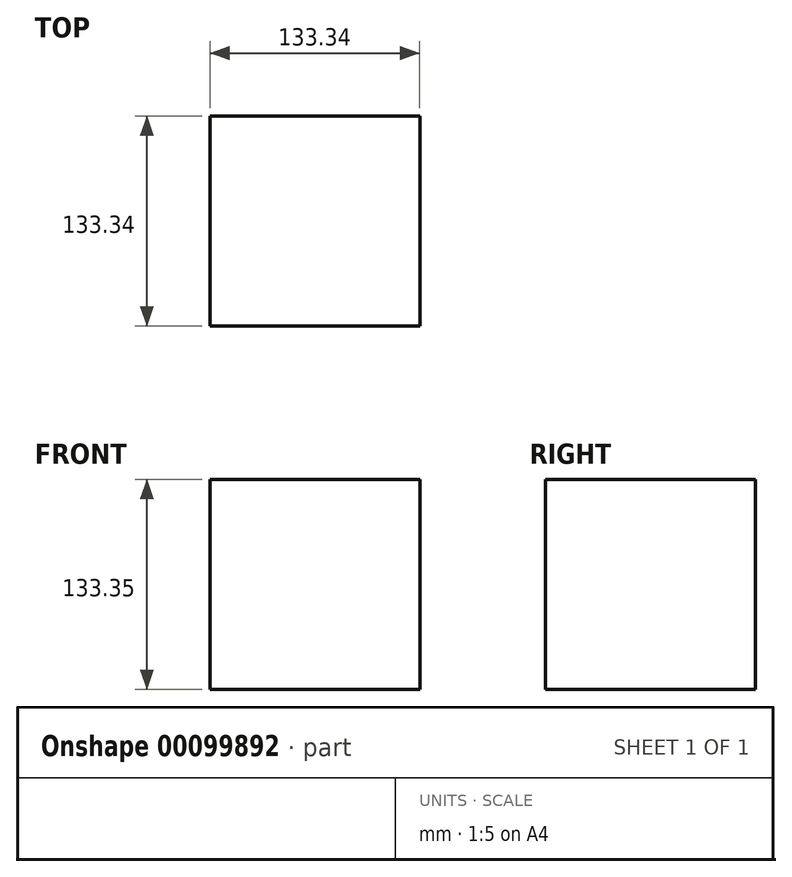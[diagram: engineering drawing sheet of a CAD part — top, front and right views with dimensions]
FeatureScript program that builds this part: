
annotation { "Feature Type Name" : "Feature", "Feature Type Description" : "" }
export const myFeature = defineFeature(function(context is Context, id is Id, definition is map)
    precondition{}
    {
        {
            var Q0;
            Q0=qCreatedBy(makeId("Top.planeOp"),FACE);
            var sketch = newSketch(context, id + "F0", { "sketchPlane" : qUnion([Q0])});
            skLineSegment(sketch, "E0.bottom", {"start": v(66.68, 66.68) * mm, "end": v(-66.68, 66.68) * mm});
            skLineSegment(sketch, "E0.top", {"start": v(66.68, -66.68) * mm, "end": v(-66.68, -66.68) * mm});
            skLineSegment(sketch, "E0.left", {"start": v(66.68, 66.68) * mm, "end": v(66.68, -66.68) * mm});
            skLineSegment(sketch, "E0.right", {"start": v(-66.68, 66.68) * mm, "end": v(-66.68, -66.68) * mm});
            skPoint(sketch, "E0.middle", {"position": v(0, 0) * mm});
            skSolve(sketch);
        }
        {
            var Q0;
            Q0 = qSketchRegion(id + "F0", true);
            extrude(context, id + "F1", {"entities" : qUnion([Q0]), "depth" : 133.35 * mm});
        }
    });
